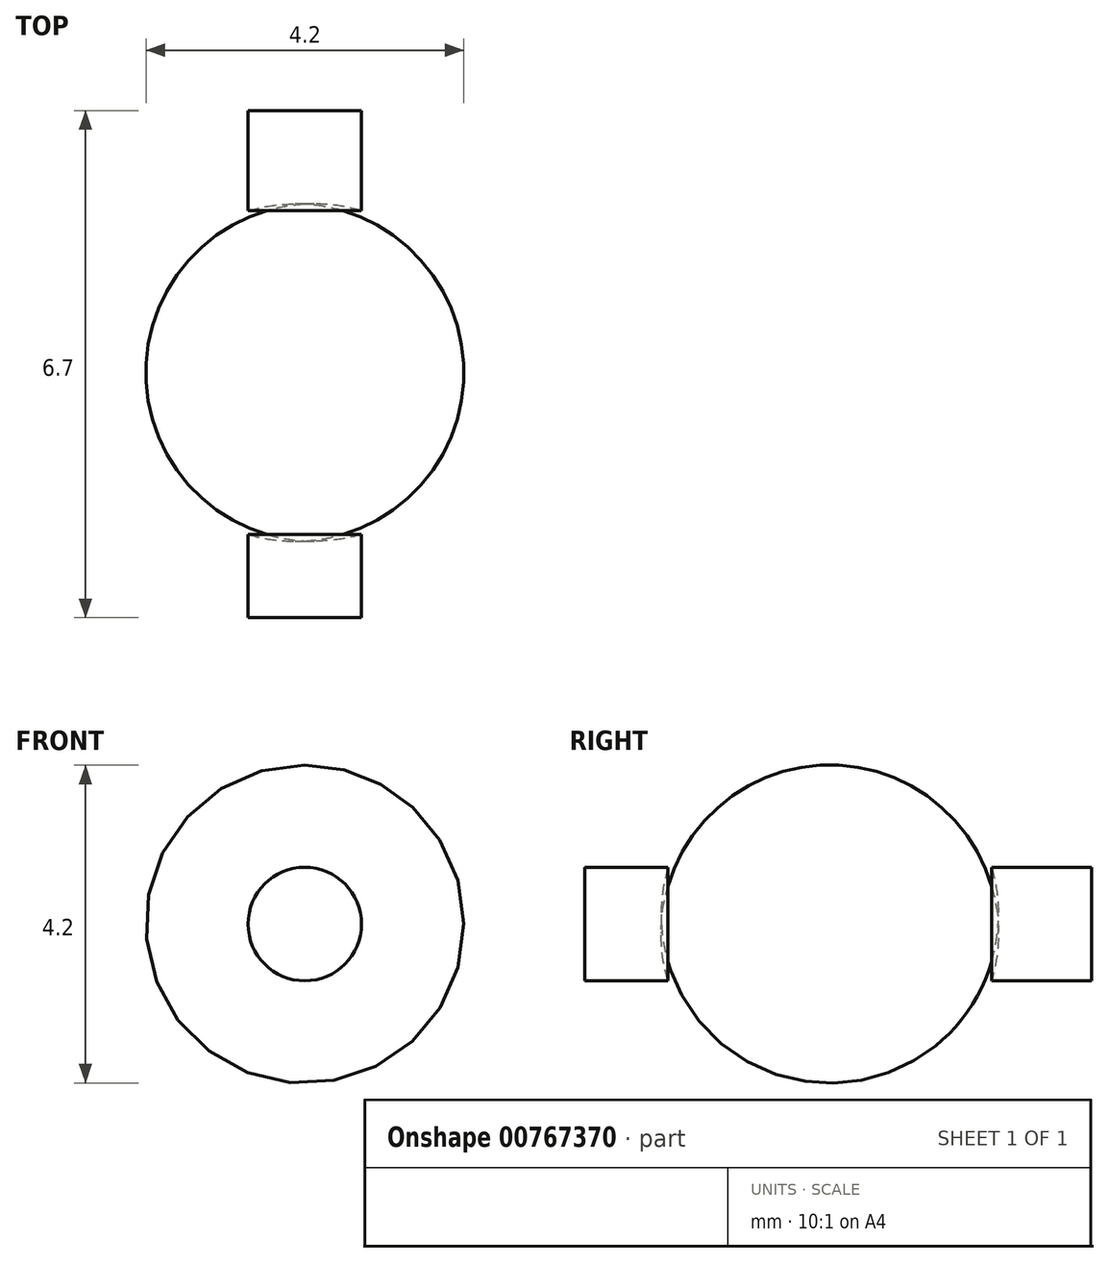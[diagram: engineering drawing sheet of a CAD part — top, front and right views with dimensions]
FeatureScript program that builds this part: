
annotation { "Feature Type Name" : "Feature", "Feature Type Description" : "" }
export const myFeature = defineFeature(function(context is Context, id is Id, definition is map)
    precondition{}
    {
        {
            var Q0;
            Q0=qCreatedBy(makeId("Front.planeOp"),FACE);
            var sketch = newSketch(context, id + "F0", { "sketchPlane" : qUnion([Q0])});
            skCircle(sketch, "E0", {"center": v(0, 0) * mm, "radius": 0.75 * mm});
            skSolve(sketch);
        }
        {
            var Q0;
            Q0 = qSketchRegion(id + "F0", true);
            extrude(context, id + "F1", {"entities" : qUnion([Q0]), "endBound" : BoundingType.SYMMETRIC, "depth" : 6.7 * mm, "offsetDistance" : 25 * mm});
        }
        {
            var Q0;
            Q0=qCreatedBy(makeId("Right.planeOp"),FACE);
            var sketch = newSketch(context, id + "F2", { "sketchPlane" : qUnion([Q0])});
            skCircle(sketch, "E1", {"center": v(0, 0) * mm, "radius": 0.75 * mm});
            skSolve(sketch);
        }
        {
            var Q0;
            Q0 = qSketchRegion(id + "F2", true);
            extrude(context, id + "F3", {"entities" : qUnion([Q0]), "operationType" : NewBodyOperationType.ADD, "endBound" : BoundingType.SYMMETRIC, "depth" : 6.7 * mm, "offsetDistance" : 25 * mm});
        }
        {
            var Q0;
            Q0=qCreatedBy(makeId("Top.planeOp"),FACE);
            var sketch = newSketch(context, id + "F4", { "sketchPlane" : qUnion([Q0])});
            skLineSegment(sketch, "E2", {"start": v(0, -2.34) * mm, "end": v(0, 2.11) * mm});
            skArc(sketch, "E3", {"start": v(0, -2.34) * mm, "mid": v(2.35, -0.11) * mm, "end": v(0, 2.11) * mm});
            skSolve(sketch);
        }
        {
            var Q0;
            Q0 = qSketchRegion(id + "F4", true);
            var Q1;
            Q1=sQuery(id+"F4.wireOp",EDGE,"E2");
            var Q2;
            Q2=sQuery(id+"F4.wireOp",EDGE,"E2");
            revolve(context, id + "F5", {"operationType" : NewBodyOperationType.ADD, "surfaceOperationType" : NewSurfaceOperationType.NEW, "entities" : qUnion([Q0]), "surfaceEntities" : qUnion([Q1]), "axis" : qUnion([Q2]), "revolveType" : RevolveType.FULL});
        }
    });
